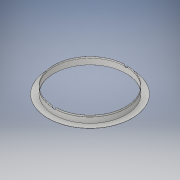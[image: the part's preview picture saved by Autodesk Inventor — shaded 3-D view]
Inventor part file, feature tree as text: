
AUTODESK INVENTOR PART (.ipt)
format: ipt  version: 2017 (Build 210142000, 142)  size: 153,600 bytes
history: native  units: in
note: dims shown in document units (in); Inventor stores cm internally (conversion verified against a paired STEP export)
features: sketch x2, revolve x1, plane x1, extrude x1
ambient origin geometry x8: Origin, YZ Plane, XZ Plane, XY Plane, X Axis, Y Axis, Z Axis, Center Point
bodies: Solid1 (feature_tree)
feature tree (5):
  revolve  "Revolution1"  [1 undecoded]
  plane  "Work Plane1"
  extrude  "Extrusion1"  Depth=0.5in
  sketch  "Sketch1"  dims[d0=1.05in d1=5.875in]
  sketch  "Sketch2"  dims[d2=1.0in d3=0.0312in d4=0.9688in d5=0.125in d6=0.25in d7=90.0deg d8=0.125in d9=0.0in d10=0.5in d11=1.0in d12=0.0in]
note: 1 required parameter value undecoded (feature->parameter linkage not recoverable at this tier; creation-order binding heuristic only, values carry confidence <= 0.55)
